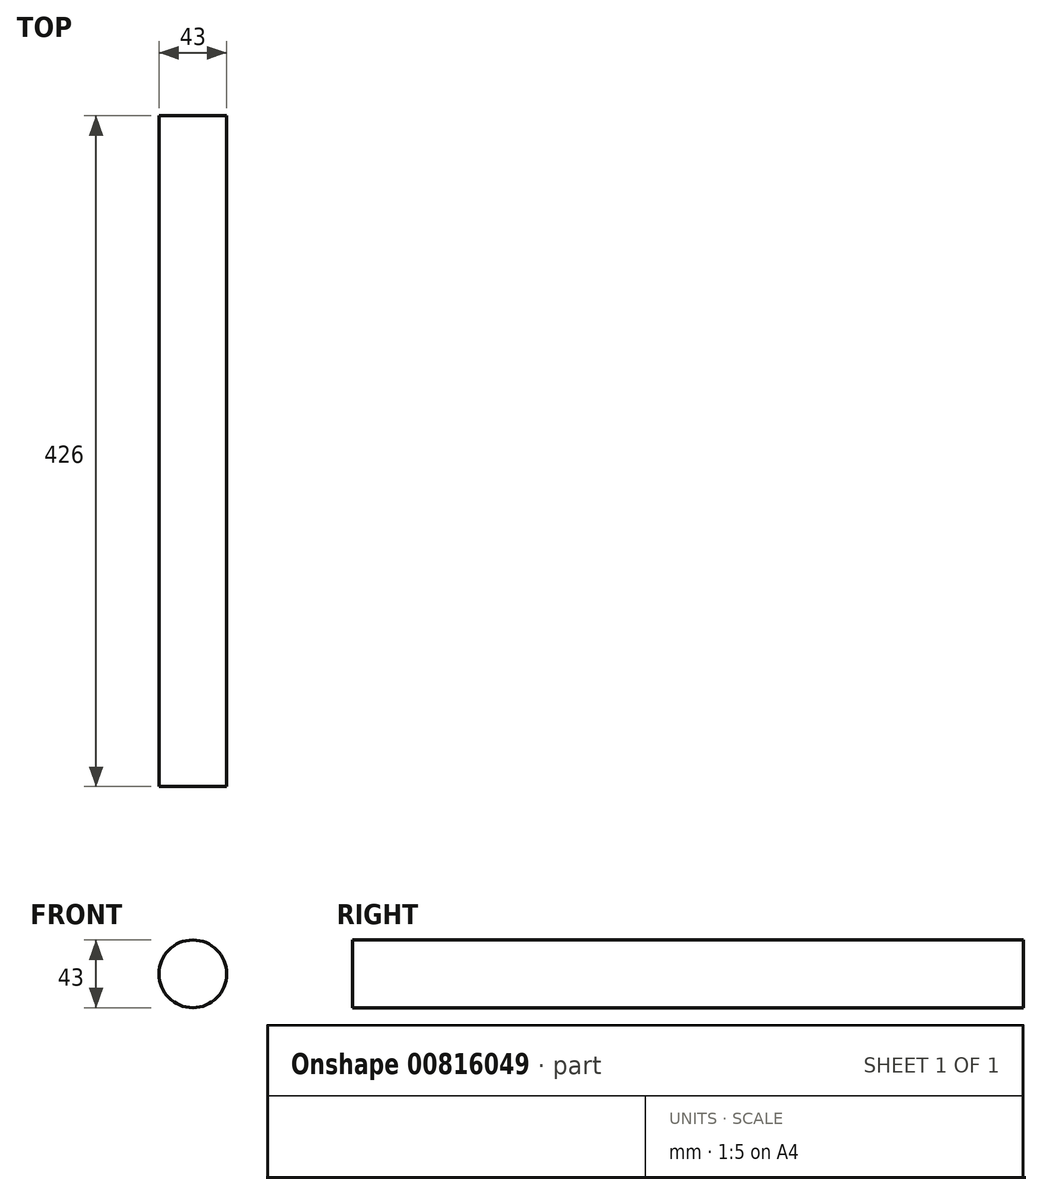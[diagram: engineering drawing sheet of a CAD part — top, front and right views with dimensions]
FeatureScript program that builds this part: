
annotation { "Feature Type Name" : "Feature", "Feature Type Description" : "" }
export const myFeature = defineFeature(function(context is Context, id is Id, definition is map)
    precondition{}
    {
        {
            var Q0;
            Q0=qCreatedBy(makeId("Front.planeOp"),FACE);
            var sketch = newSketch(context, id + "F0", { "sketchPlane" : qUnion([Q0])});
            skCircle(sketch, "E0", {"center": v(0, 0) * mm, "radius": 21.5 * mm});
            skSolve(sketch);
        }
        {
            var Q0;
            Q0=makeQuery(id+"F0.imprint","IMPRINT",FACE,{"disambiguationData":[TD([[makeQuery(id+"F0.imprint","IMPRINT",EDGE,{"derivedFrom":sQuery(id+"F0.wireOp",EDGE,"E0")}),1.0]])]});
            extrude(context, id + "F1", {"entities" : qUnion([Q0]), "depth" : 426 * mm, "offsetDistance" : 25 * mm});
        }
    });
